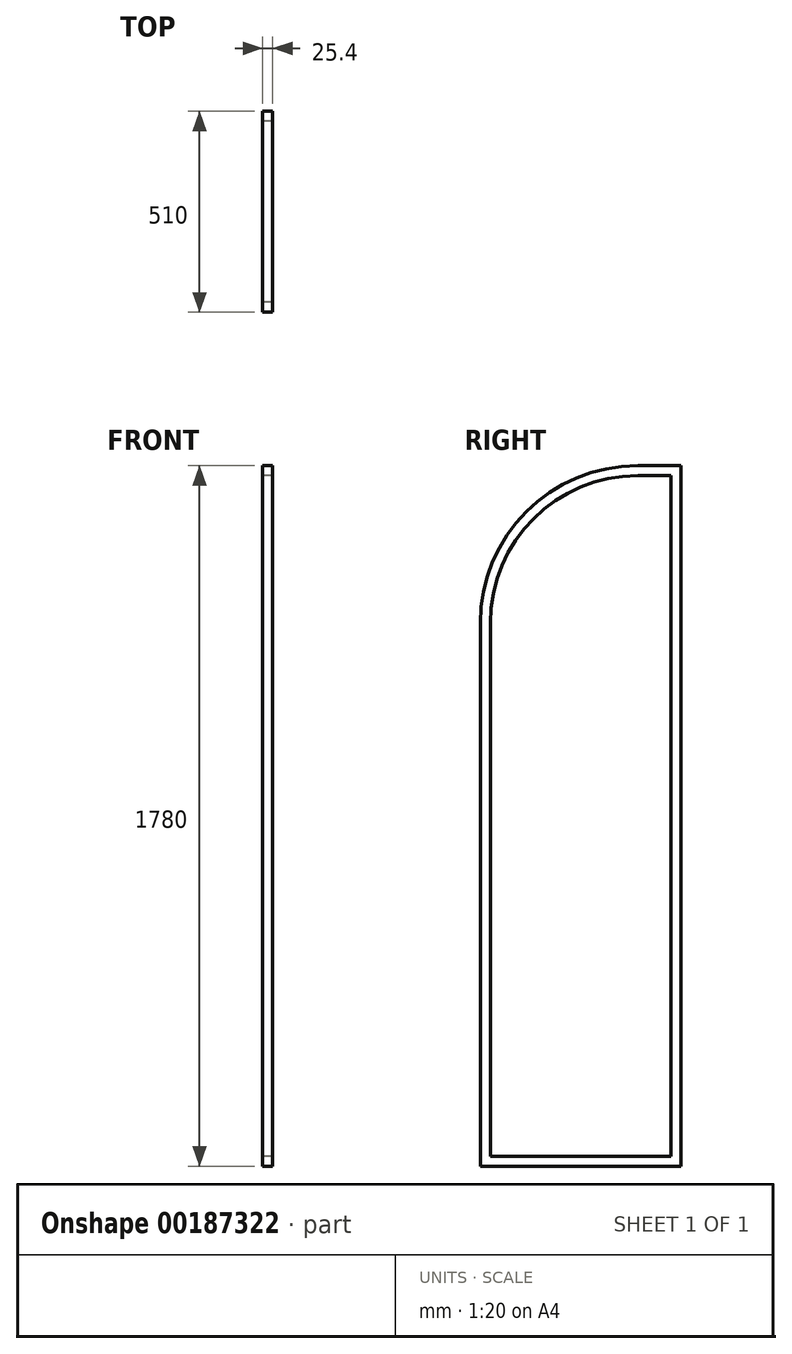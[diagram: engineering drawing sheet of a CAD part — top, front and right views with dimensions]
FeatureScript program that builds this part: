
annotation { "Feature Type Name" : "Feature", "Feature Type Description" : "" }
export const myFeature = defineFeature(function(context is Context, id is Id, definition is map)
    precondition{}
    {
        {
            var Q0;
            Q0=qCreatedBy(makeId("Right.planeOp"),FACE);
            var sketch = newSketch(context, id + "F0", { "sketchPlane" : qUnion([Q0])});
            skLineSegment(sketch, "E0.bottom", {"start": v(255, 890) * mm, "end": v(145, 890) * mm});
            skLineSegment(sketch, "E0.top", {"start": v(255, -890) * mm, "end": v(-255, -890) * mm});
            skLineSegment(sketch, "E0.left", {"start": v(255, 890) * mm, "end": v(255, -890) * mm});
            skLineSegment(sketch, "E0.right", {"start": v(-255, 490) * mm, "end": v(-255, -890) * mm});
            skPoint(sketch, "E0.middle", {"position": v(0, 0) * mm});
            skPoint(sketch, "E1.visualSharp", {"position": v(-255, 890) * mm});
            skArc(sketch, "E1.filletArc", {"start": v(145, 890) * mm, "mid": v(-137.84, 772.84) * mm, "end": v(-255, 490) * mm});
            skArc(sketch, "E2.0", {"start": v(145, 864.6) * mm, "mid": v(-119.88, 754.88) * mm, "end": v(-229.6, 490) * mm});
            skLineSegment(sketch, "E2.1", {"start": v(229.6, 864.6) * mm, "end": v(145, 864.6) * mm});
            skLineSegment(sketch, "E2.2", {"start": v(-229.6, 490) * mm, "end": v(-229.6, -864.6) * mm});
            skLineSegment(sketch, "E2.3", {"start": v(229.6, -864.6) * mm, "end": v(-229.6, -864.6) * mm});
            skLineSegment(sketch, "E2.4", {"start": v(229.6, 864.6) * mm, "end": v(229.6, -864.6) * mm});
            skSolve(sketch);
        }
        {
            var Q0;
            Q0 = qSketchRegion(id + "F0", true);
            extrude(context, id + "F1", {"entities" : qUnion([Q0]), "endBound" : BoundingType.SYMMETRIC, "depth" : 25.4 * mm});
        }
    });
